# Revit family: QF_MACOM_HOSIM65NELM-2M
name_source: partatom
category: Equipamento especial
units: mm (PartAtom-declared; Revit-internal decimal feet)

## family parameters
Com base no plano de trabalho = Não
Compartilhado = Não
Corte com vazios quando carregada = Não
Cota do conector redondo = Utilizar diâmetro
Número OmniClass = 23.40.40.14.27
Ponto de cálculo do ambiente = Não
Sempre na vertical = Sim
Tipo de parte = Normal
Título OmniClass = Ice Machines

## types (1)
- HOSIM65NELM-2M
    Cold Water Connection Height = 766 mm
    Cold Water Flow = 0,0 L/s
    Cold Water Maximum Pressure = 0,0 Pa
    Cold Water Minimum Pressure = 0,0 Pa
    Cold Water RI Height = 0 mm
    Cold Water Size = 1"
    Cold Water Temperature Recommended = 0 °C
    Descrição = MAQUINA DE GELO EM CUBO GRANDE (48X48X58MM) HOSHIZAKI, PRODUCAO ATE 33KG/DIA, DEPOSITO DE 26KG - 220V MONOF - IM-65NE-LM-633X506X860mm
    Elec Conn RI Height = 0 mm
    Elevação padrão = 0 mm
    Fabricante = MACOM
    Indirect Waste Connection Height = 177 mm
    Indirect Waste Flow = 0,0 L/s
    Indirect Waste Size = 1"
    Max Overcurrent Protection = 0 A
    Min Ckt Capacity = 0 A
    Modelo = HOSIM65NELM-2M
HOSIM65NELM-2M
HOSIM65NELM-2M
    Number of Poles = 0
    URL = https://www.acosmacom.com.br
    Volume = 0,30 m³
    Waste Water Discharge Temperature = 0 °C

## geometry (parser evidence)
native form markers: Blend x4, Sweep x6
no freeform markers — native parametric forms only
